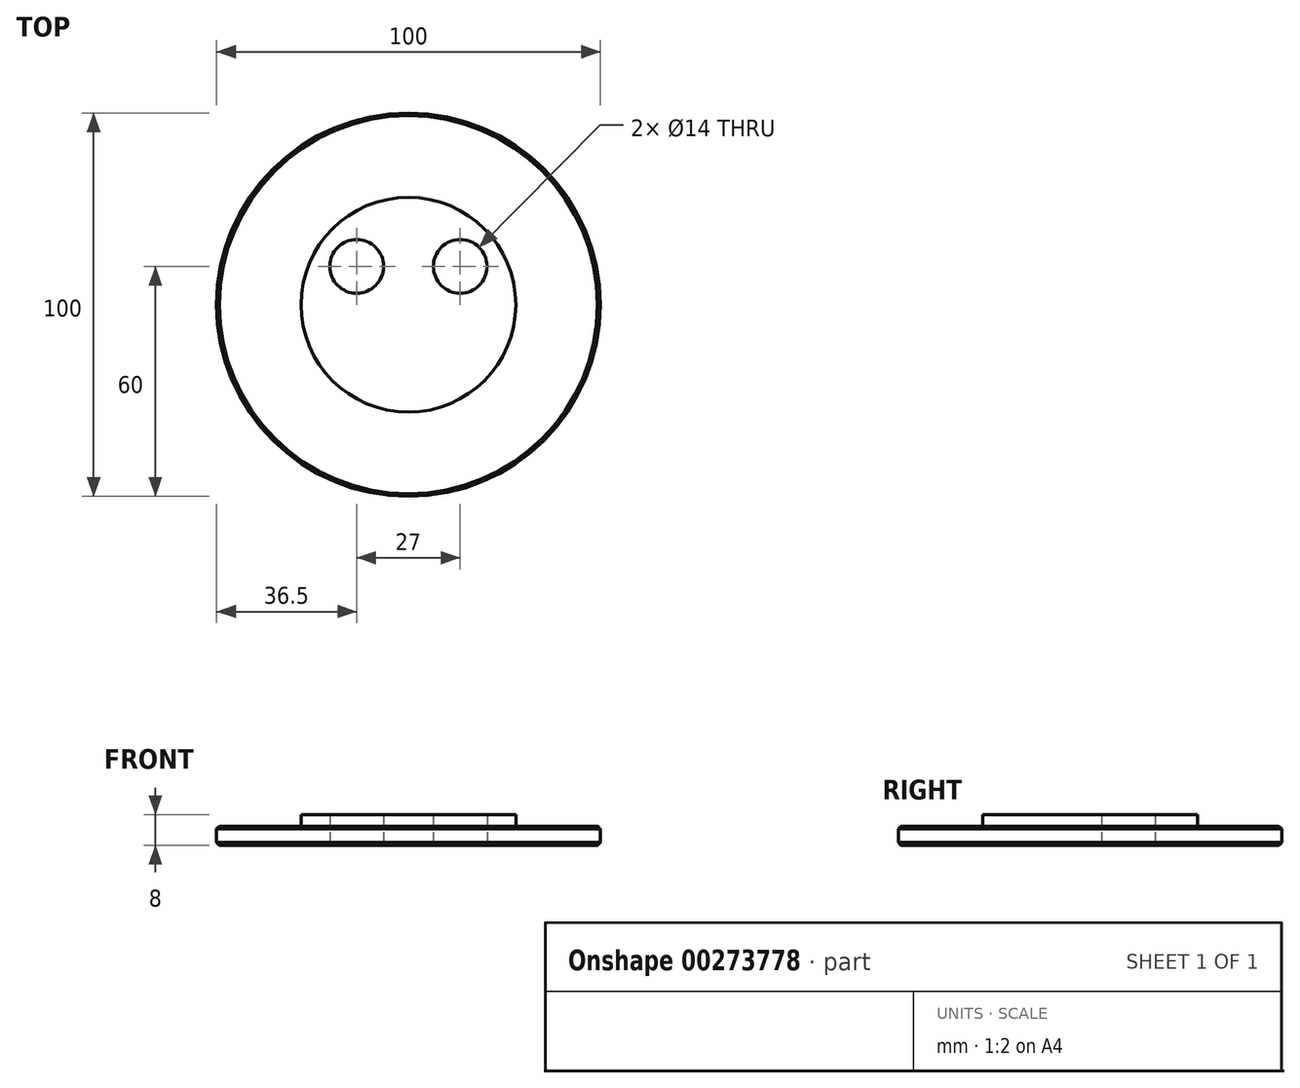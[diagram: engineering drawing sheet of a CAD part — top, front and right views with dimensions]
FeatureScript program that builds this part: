
annotation { "Feature Type Name" : "Feature", "Feature Type Description" : "" }
export const myFeature = defineFeature(function(context is Context, id is Id, definition is map)
    precondition{}
    {
        {
            var Q0;
            Q0=qCreatedBy(makeId("Top.planeOp"),FACE);
            var sketch = newSketch(context, id + "F0", { "sketchPlane" : qUnion([Q0])});
            skCircle(sketch, "E0", {"center": v(0, 0) * mm, "radius": 50 * mm});
            skCircle(sketch, "E1", {"center": v(-13.5, 10) * mm, "radius": 7 * mm});
            skCircle(sketch, "E2", {"center": v(13.5, 10) * mm, "radius": 7 * mm});
            skSolve(sketch);
        }
        {
            var Q0;
            Q0=makeQuery(id+"F0.imprint","IMPRINT",FACE,{"disambiguationData":[TD([[makeQuery(id+"F0.imprint","IMPRINT",EDGE,{"derivedFrom":sQuery(id+"F0.wireOp",EDGE,"E0")}),1.0]])]});
            extrude(context, id + "F1", {"entities" : qUnion([Q0]), "depth" : 5 * mm});
        }
        {
            var Q0;
            Q0=makeQuery(id+"F1.opExtrude","CAP_EDGE",EDGE,{"disambiguationData":[OSD([sQuery(id+"F0.wireOp",EDGE,"E0")])],"isStart":true});
            var Q1;
            Q1=makeQuery(id+"F1.opExtrude","SWEPT_FACE",FACE,{"disambiguationData":[OSD([sQuery(id+"F0.wireOp",EDGE,"E0")])]});
            chamfer(context, id + "F2", {"entities" : qUnion([Q0, Q1]), "width" : 0.7 * mm, "tangentPropagation" : true});
        }
        {
            var Q0;
            Q0=makeQuery(id+"F1.opExtrude","CAP_FACE",FACE,{"disambiguationData":[OSD([sQuery(id+"F0.wireOp",EDGE,"E0"),sQuery(id+"F0.wireOp",EDGE,"E1"),sQuery(id+"F0.wireOp",EDGE,"E2")])],"isStart":false});
            var sketch = newSketch(context, id + "F3", { "sketchPlane" : qUnion([Q0])});
            skCircle(sketch, "E3", {"center": v(0, 0) * mm, "radius": 28 * mm});
            skSolve(sketch);
        }
        {
            var Q0;
            Q0 = qSketchRegion(id + "F3", true);
            extrude(context, id + "F4", {"entities" : qUnion([Q0]), "operationType" : NewBodyOperationType.ADD, "depth" : 3 * mm});
        }
        {
            var Q0;
            Q0=makeQuery(id+"F4.boolean.opBoolean","SPLIT",FACE,{"disambiguationData":[TD([makeQuery(id+"F1.opExtrude","SWEPT_FACE",FACE,{"disambiguationData":[OSD([sQuery(id+"F0.wireOp",EDGE,"E1")])]})])],"derivedFrom":makeQuery(id+"F4.opExtrude","CAP_FACE",FACE,{"disambiguationData":[OSD([sQuery(id+"F3.wireOp",EDGE,"E3")])],"isStart":true})});
            var Q1;
            Q1=makeQuery(id+"F4.boolean.opBoolean","SPLIT",FACE,{"disambiguationData":[TD([makeQuery(id+"F1.opExtrude","SWEPT_FACE",FACE,{"disambiguationData":[OSD([sQuery(id+"F0.wireOp",EDGE,"E2")])]})])],"derivedFrom":makeQuery(id+"F4.opExtrude","CAP_FACE",FACE,{"disambiguationData":[OSD([sQuery(id+"F3.wireOp",EDGE,"E3")])],"isStart":true})});
            extrude(context, id + "F5", {"entities" : qUnion([Q0, Q1]), "operationType" : NewBodyOperationType.REMOVE, "endBound" : BoundingType.UP_TO_NEXT, "oppositeDirection" : true, "depth" : 25 * mm});
        }
    });
